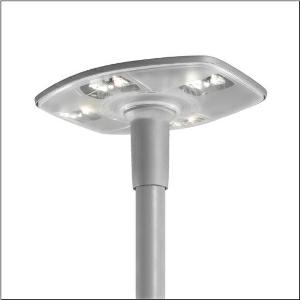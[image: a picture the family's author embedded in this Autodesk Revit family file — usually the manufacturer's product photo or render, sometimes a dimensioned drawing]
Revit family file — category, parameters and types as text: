
# Revit family: dl_30_led___st1_2c_5xa513271b08a5_d9bb
name_source: partatom
category: Lighting Fixtures
units: mm (PartAtom-declared; Revit-internal decimal feet)

## family parameters
Cut with Voids When Loaded = No
Host = Face
Light Source = No
Part Type = Normal
Room Calculation Point = No
Round Connector Dimension = Use Diameter
Shared = No

## types (1)
- --- (1 x LED, 5540 lm, 48.9 W, 4000K)
    Apparent Load = 49 VA
    CIE Flux Codes = 32 71 98 100 100
    Color Rendering = 70
    Color Temperature = 4000K
    Default Elevation = 1800 mm
    Description = DL 30 LED, mast luminaire, primary light control with 3 zone facetted reflector, of plastic, aluminium vaporised, highly specular, primary optical cover: cover, of PMMA, structured, transparent, light distribution: ST1.2c, light emission: direct distribution, primary light characteristic: asymmetric, crossroads, installation type: post-top, LED, High Power LED, rated luminous flux: 5.540lm, luminous efficacy: 113lm/W, light colour: 740, colour temperature: 4000K, control gear: Plus, control: flexible luminous flux parameterisation, time-dependent luminous flux control, constant luminous flux control, digital communication interface, power reduction, electronic power reduction, mains connection: 230..240V, AC, 50/60Hz, start of lifetime: 49W, end of service life: 51W, reduction: 23W, luminaire housing, of diecast aluminium, powder-coated, SITECO metallic grey (DB 702S), length: 600mm, width: 510mm, height: 290mm, spigot size: d x l = 76 x 100mm (post-top) | with reducer (optional accessory) 60 x 100mm, mounting height: 3..6m, protection rating (complete): IP66, insulation class (complete): insulation class II (safety insulation), certification: CE, ENEC, VDE, impact resistance: IK08, permissible operating ambient temperature: -25..+30°C, standard-compliant lighting for roads and squares, packaging unit: 1 piece

Light Distribution: ST1.2c
    Height = 290 mm
    Lamp = 1 x LED
    Lamp Light Flux = 5540 lm
    Lamp Power = 48.9 W
    Lamp count = 1
    Length = 510 mm
    Luminous efficacy = 113 lm/W
    Manufacturer = Siteco
    ModVariant = No
    Model = 5XA513271B08A5
    Mounting Place = Pole
    Mounting Type = Pole top
    Number of Poles = 1
    OnlyDefault = Yes
    Power Factor = 1
    Product Name = DL 30 LED | ST1.2c
    Product group = mast luminaire | pylon top
    ProductGroupID = 6100
    Protection Class = Protection class II
    Protection Degree = IP 66
    RLX_Detail_Level = 1
    RLX_Emergency_Light_Flux = 0 lm
    RLX_Emergency_Type = 0
    RLX_Emergency_Type_DB = No
    RlxData = <blob elided: 86409 chars, md5=7d4a62f8>
    Socket = socket
    Standby Power = 0 W
    System Light Flux = 5540 lm
    System Power = 49 W
    Type Comments = factory setting: luminous flux: 100 % | dim-lin: 254 | 497 mA
    Type Image = l_1006003.jpg
    URL = http://relux.com
    VarID = @adj_196913
    Voltage = 0 V
    Weight = 0.00 kg
    Width = 600 mm

## geometry (parser evidence)
native form markers: Blend x4, Sweep x10
no freeform markers — native parametric forms only
